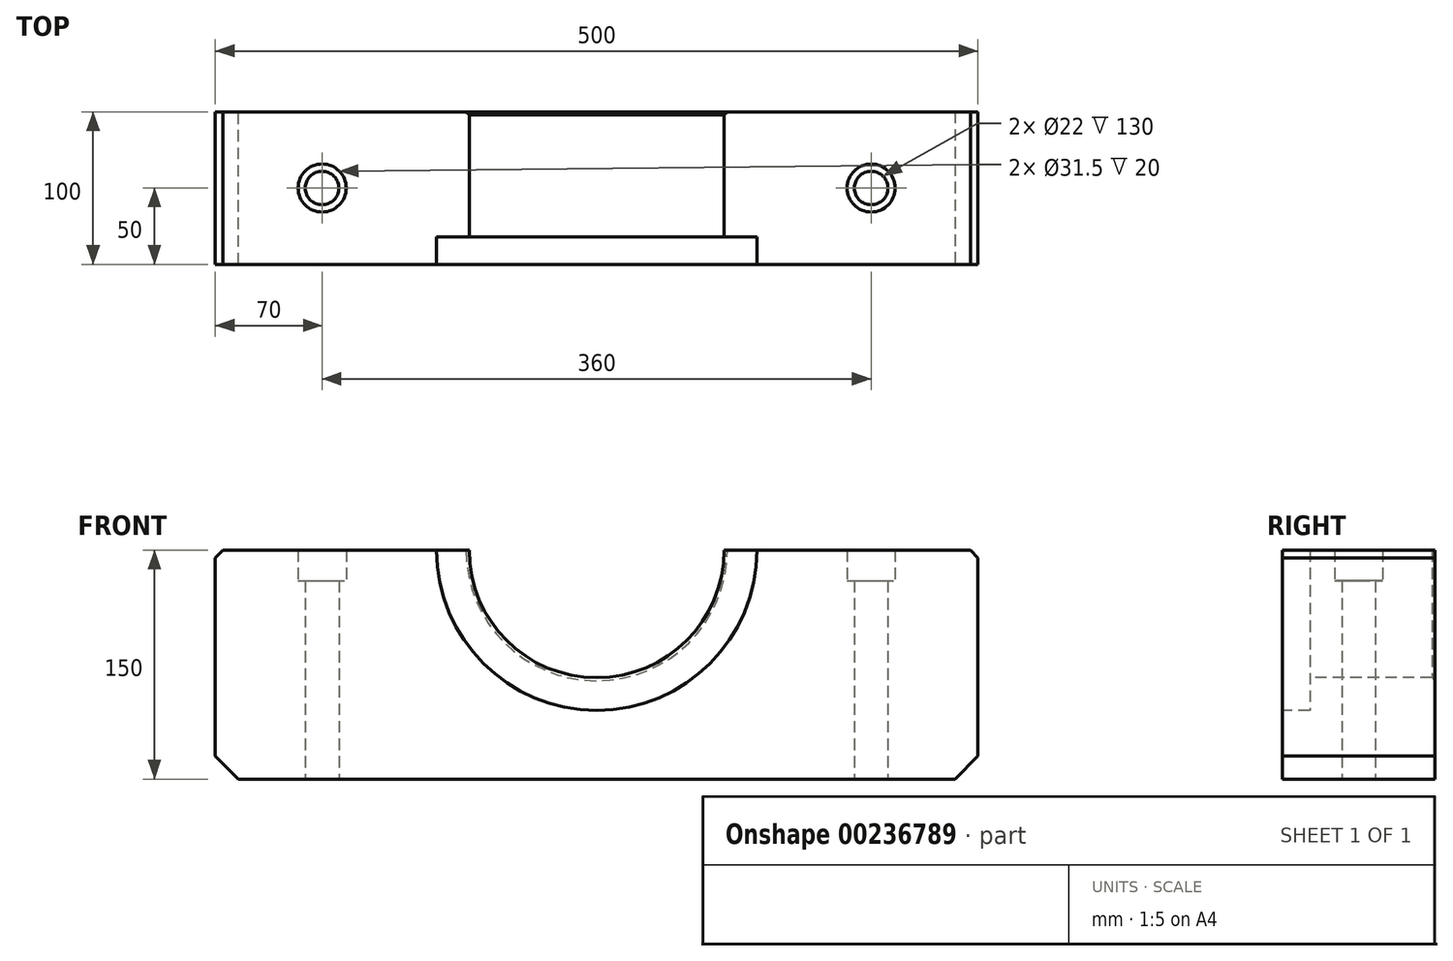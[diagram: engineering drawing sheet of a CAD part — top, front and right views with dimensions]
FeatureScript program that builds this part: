
annotation { "Feature Type Name" : "Feature", "Feature Type Description" : "" }
export const myFeature = defineFeature(function(context is Context, id is Id, definition is map)
    precondition{}
    {
        {
            var Q0;
            Q0=qCreatedBy(makeId("Top.planeOp"),FACE);
            var sketch = newSketch(context, id + "F0", { "sketchPlane" : qUnion([Q0])});
            skLineSegment(sketch, "E0.bottom", {"start": v(0, 0) * mm, "end": v(500, 0) * mm});
            skLineSegment(sketch, "E0.top", {"start": v(0, 100) * mm, "end": v(500, 100) * mm});
            skLineSegment(sketch, "E0.left", {"start": v(0, 0) * mm, "end": v(0, 100) * mm});
            skLineSegment(sketch, "E0.right", {"start": v(500, 0) * mm, "end": v(500, 100) * mm});
            skSolve(sketch);
        }
        {
            var Q0;
            Q0=qSketchRegion(id+"F0",true);
            extrude(context, id + "F1", {"entities" : qUnion([Q0]), "depth" : 150 * mm, "offsetDistance" : 25 * mm});
        }
        {
            var Q0;
            Q0=makeQuery(id+"F1.opExtrude","SWEPT_FACE",FACE,{"disambiguationData":[OSD([sQuery(id+"F0.wireOp",EDGE,"E0.bottom")])]});
            var sketch = newSketch(context, id + "F2", { "sketchPlane" : qUnion([Q0])});
            skCircle(sketch, "E1", {"center": v(250, 150) * mm, "radius": 83.6 * mm});
            skPoint(sketch, "E1.centerSnap0", {"position": v(500, 75) * mm});
            skPoint(sketch, "E1.centerSnap1", {"position": v(250, 150) * mm});
            skSolve(sketch);
        }
        {
            var Q0;
            Q0=makeQuery(id+"F2.imprint","IMPRINT",FACE,{"disambiguationData":[TD([[makeQuery(id+"F2.imprint","IMPRINT",EDGE,{"derivedFrom":sQuery(id+"F2.wireOp",EDGE,"E1")}),1.0]])]});
            extrude(context, id + "F3", {"entities" : qUnion([Q0]), "operationType" : NewBodyOperationType.REMOVE, "endBound" : BoundingType.THROUGH_ALL, "oppositeDirection" : true, "depth" : 25 * mm, "offsetDistance" : 25 * mm});
        }
        {
            var Q0;
            Q0=makeQuery(id+"F1.opExtrude","SWEPT_FACE",FACE,{"disambiguationData":[OSD([sQuery(id+"F0.wireOp",EDGE,"E0.bottom")])]});
            var sketch = newSketch(context, id + "F4", { "sketchPlane" : qUnion([Q0])});
            skCircle(sketch, "E2", {"center": v(250, 150) * mm, "radius": 105 * mm});
            skSolve(sketch);
        }
        {
            var Q0;
            Q0=qSketchRegion(id+"F4",true);
            extrude(context, id + "F5", {"entities" : qUnion([Q0]), "operationType" : NewBodyOperationType.REMOVE, "oppositeDirection" : true, "depth" : 18 * mm, "offsetDistance" : 25 * mm});
        }
        {
            var Q0;
            Q0=makeQuery(id+"F3.boolean.opBoolean","INTERSECT",EDGE,{"derivedFrom":[makeQuery(id+"F1.opExtrude","SWEPT_FACE",FACE,{"disambiguationData":[OSD([sQuery(id+"F0.wireOp",EDGE,"E0.top")])]}),makeQuery(id+"F3.opExtrude","SWEPT_FACE",FACE,{"disambiguationData":[OSD([sQuery(id+"F2.wireOp",EDGE,"E1")])]})]});
            chamfer(context, id + "F6", {"entities" : qUnion([Q0]), "width" : 2 * mm, "tangentPropagation" : true});
        }
        {
            var Q0;
            Q0=makeQuery(id+"F1.opExtrude","CAP_EDGE",EDGE,{"disambiguationData":[OSD([sQuery(id+"F0.wireOp",EDGE,"E0.right")])],"isStart":false});
            var Q1;
            Q1=makeQuery(id+"F1.opExtrude","CAP_EDGE",EDGE,{"disambiguationData":[OSD([sQuery(id+"F0.wireOp",EDGE,"E0.left")])],"isStart":false});
            chamfer(context, id + "F7", {"entities" : qUnion([Q0, Q1]), "width" : 5 * mm, "tangentPropagation" : true});
        }
        {
            var Q0;
            Q0=makeQuery(id+"F1.opExtrude","CAP_FACE",FACE,{"disambiguationData":[OSD([sQuery(id+"F0.wireOp",EDGE,"E0.bottom"),sQuery(id+"F0.wireOp",EDGE,"E0.top"),sQuery(id+"F0.wireOp",EDGE,"E0.left"),sQuery(id+"F0.wireOp",EDGE,"E0.right")])],"isStart":false});
            var sketch = newSketch(context, id + "F8", { "sketchPlane" : qUnion([Q0])});
            skPoint(sketch, "E3", {"position": v(70, 50) * mm});
            skPoint(sketch, "E4", {"position": v(430, 50) * mm});
            skSolve(sketch);
        }
        {
            var Q0;
            Q0=sQuery(id+"F8.wireOp",VERTEX,"E3");
            var Q1;
            Q1=sQuery(id+"F8.wireOp",VERTEX,"E4");
            var Q2;
            Q2=makeQuery(id+"F1.opExtrude","SWEPT_BODY",BODY,{"disambiguationData":[OSD([sQuery(id+"F0.wireOp",EDGE,"E0.bottom"),sQuery(id+"F0.wireOp",EDGE,"E0.top"),sQuery(id+"F0.wireOp",EDGE,"E0.left"),sQuery(id+"F0.wireOp",EDGE,"E0.right")])]});
            hole(context, id + "F9", {"style" : HoleStyle.C_BORE, "endStyle" : HoleEndStyle.THROUGH, "standardTappedOrClearance" : lookupTablePath({ "fit" : "Normal", "standard" : "ISO", "size" : "M20", "type" : "Clearance" }), "standardBlindInLast" : lookupTablePath({ "fit" : "Normal", "standard" : "ISO", "size" : "M20", "type" : "Clearance" }), "holeDiameter" : 22 * mm, "cBoreDiameter" : 31.5 * mm, "cBoreDepth" : 20 * mm, "majorDiameter" : 5 * mm, "isTappedThrough" : true, "tappedDepth" : 28 * mm, "tapClearance" : 3, "locations" : qUnion([Q0, Q1]), "scope" : qUnion([Q2])});
        }
        {
            var Q0;
            Q0=makeQuery(id+"F1.opExtrude","CAP_EDGE",EDGE,{"disambiguationData":[OSD([sQuery(id+"F0.wireOp",EDGE,"E0.right")])],"isStart":true});
            var Q1;
            Q1=makeQuery(id+"F1.opExtrude","CAP_EDGE",EDGE,{"disambiguationData":[OSD([sQuery(id+"F0.wireOp",EDGE,"E0.left")])],"isStart":true});
            chamfer(context, id + "F10", {"entities" : qUnion([Q0, Q1]), "width" : 15 * mm, "tangentPropagation" : true});
        }
    });
